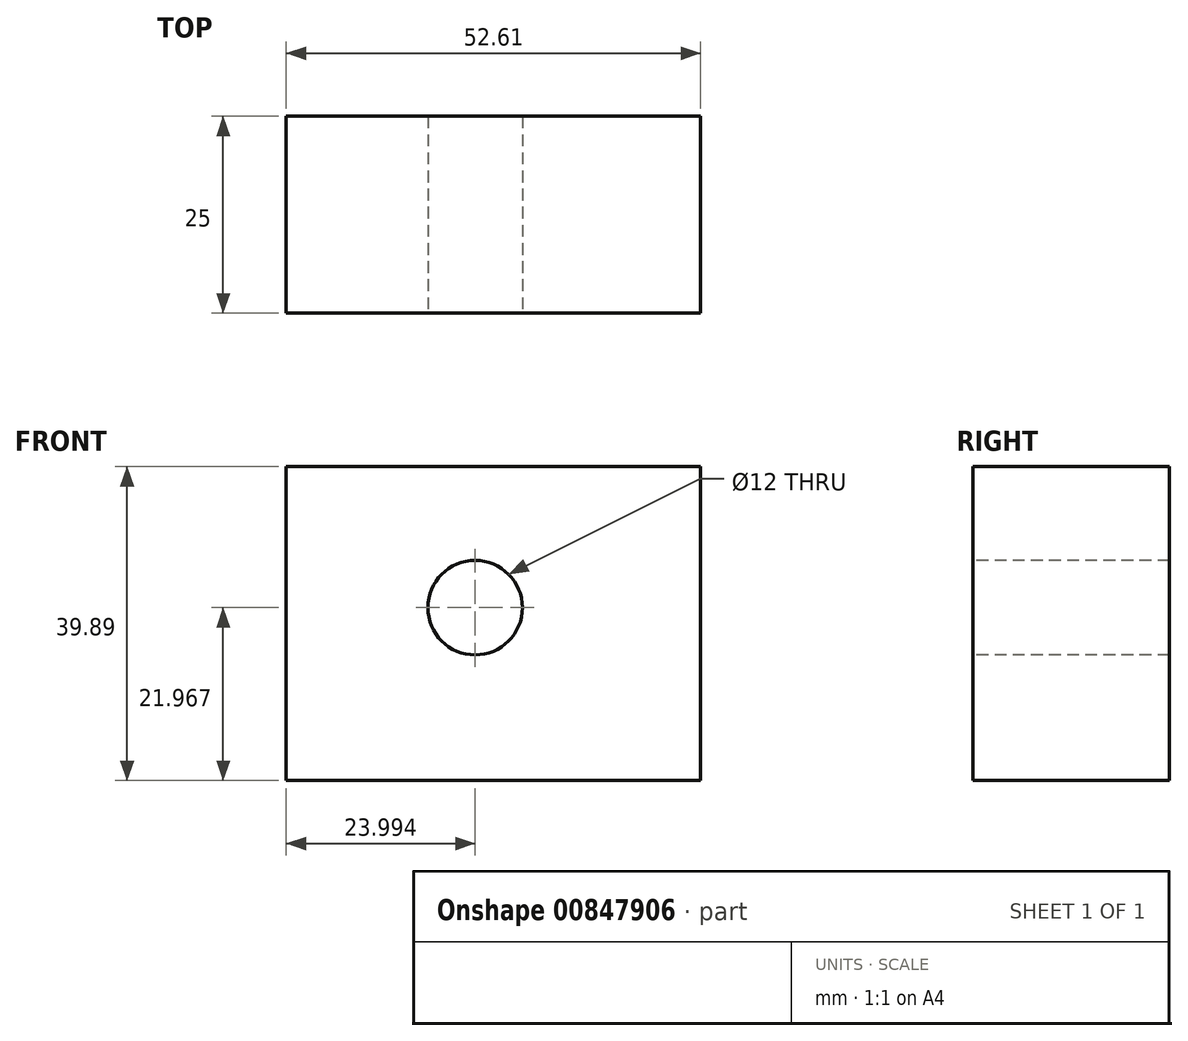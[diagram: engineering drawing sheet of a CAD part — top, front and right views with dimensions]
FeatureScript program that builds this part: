
annotation { "Feature Type Name" : "Feature", "Feature Type Description" : "" }
export const myFeature = defineFeature(function(context is Context, id is Id, definition is map)
    precondition{}
    {
        {
            var Q0;
            Q0=qCreatedBy(makeId("Front.planeOp"),FACE);
            var sketch = newSketch(context, id + "F0", { "sketchPlane" : qUnion([Q0])});
            skLineSegment(sketch, "E0.bottom", {"start": v(-119.82, 8.53) * mm, "end": v(-67.2, 8.53) * mm});
            skLineSegment(sketch, "E0.top", {"start": v(-119.82, 48.42) * mm, "end": v(-67.2, 48.42) * mm});
            skLineSegment(sketch, "E0.left", {"start": v(-119.82, 8.53) * mm, "end": v(-119.82, 48.42) * mm});
            skLineSegment(sketch, "E0.right", {"start": v(-67.2, 8.53) * mm, "end": v(-67.2, 48.42) * mm});
            skPoint(sketch, "E0.middle", {"position": v(-93.51, 28.47) * mm});
            skSolve(sketch);
        }
        {
            var Q0;
            Q0=makeQuery(id+"F0.imprint","IMPRINT",FACE,{"disambiguationData":[TD([[makeQuery(id+"F0.imprint","IMPRINT",EDGE,{"derivedFrom":sQuery(id+"F0.wireOp",EDGE,"E0.bottom")}),1.0]])]});
            extrude(context, id + "F1", {"entities" : qUnion([Q0]), "depth" : 25 * mm, "offsetDistance" : 25 * mm});
        }
        {
            var Q0;
            Q0=makeQuery(id+"F1.opExtrude","CAP_FACE",FACE,{"disambiguationData":[OSD([sQuery(id+"F0.wireOp",EDGE,"E0.bottom"),sQuery(id+"F0.wireOp",EDGE,"E0.top"),sQuery(id+"F0.wireOp",EDGE,"E0.left"),sQuery(id+"F0.wireOp",EDGE,"E0.right")])],"isStart":false});
            var sketch = newSketch(context, id + "F2", { "sketchPlane" : qUnion([Q0])});
            skPoint(sketch, "E1", {"position": v(-95.83, 30.5) * mm});
            skSolve(sketch);
        }
        {
            var Q0;
            Q0=sQuery(id+"F2.wireOp",VERTEX,"E1");
            var Q1;
            Q1=makeQuery(id+"F1.opExtrude","SWEPT_BODY",BODY,{"disambiguationData":[OSD([sQuery(id+"F0.wireOp",EDGE,"E0.bottom"),sQuery(id+"F0.wireOp",EDGE,"E0.top"),sQuery(id+"F0.wireOp",EDGE,"E0.left"),sQuery(id+"F0.wireOp",EDGE,"E0.right")])]});
            hole(context, id + "F3", {"style" : HoleStyle.SIMPLE, "endStyle" : HoleEndStyle.THROUGH, "holeDiameter" : 12 * mm, "majorDiameter" : 5 * mm, "isTappedThrough" : true, "tappedDepth" : 12 * mm, "tapClearance" : 3, "locations" : qUnion([Q0]), "scope" : qUnion([Q1])});
        }
    });
